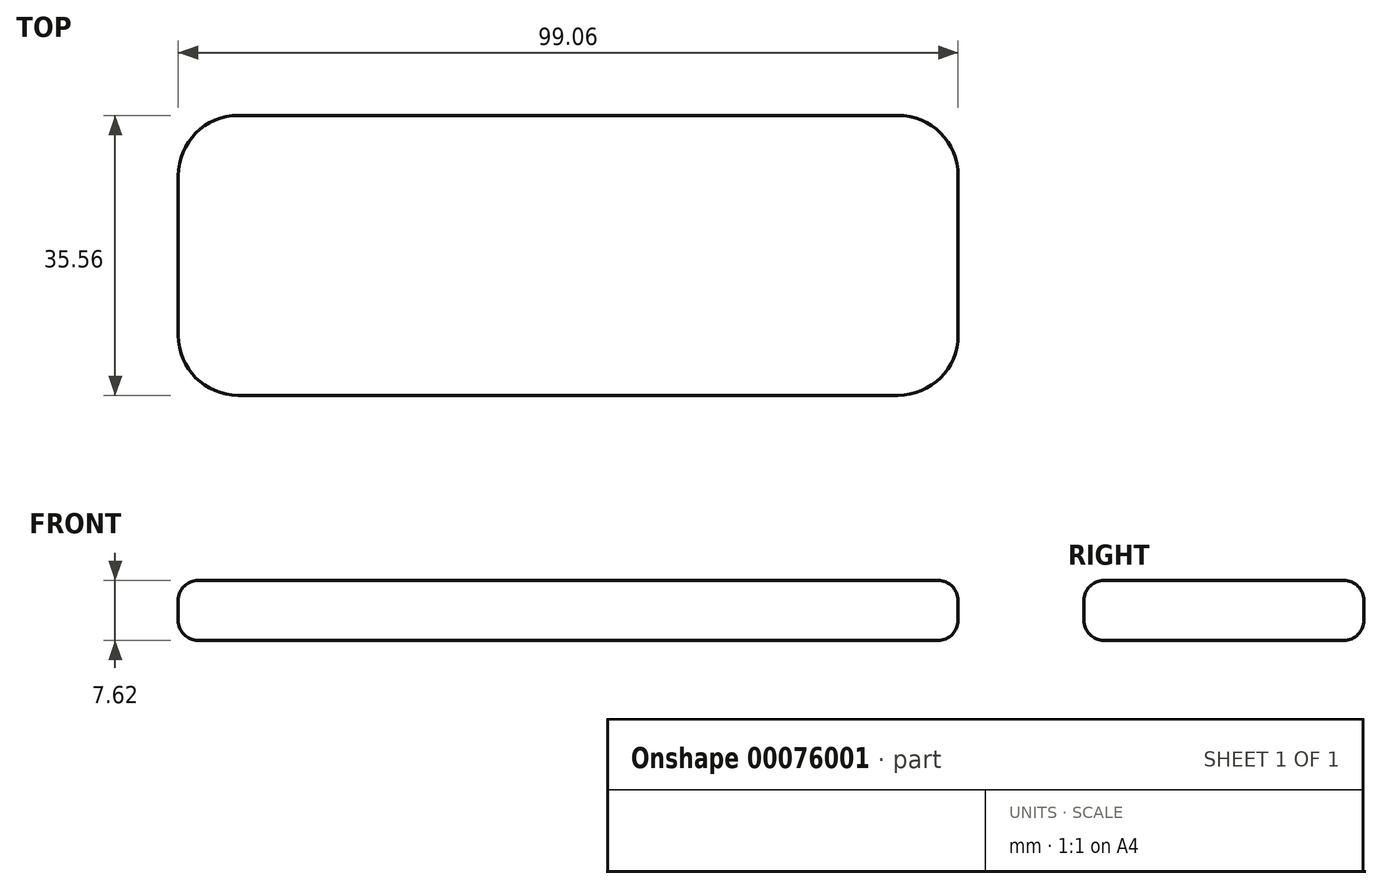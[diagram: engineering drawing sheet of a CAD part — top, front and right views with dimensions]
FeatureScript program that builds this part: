
annotation { "Feature Type Name" : "Feature", "Feature Type Description" : "" }
export const myFeature = defineFeature(function(context is Context, id is Id, definition is map)
    precondition{}
    {
        {
            var Q0;
            Q0=qCreatedBy(makeId("Top.planeOp"),FACE);
            var sketch = newSketch(context, id + "F0", { "sketchPlane" : qUnion([Q0])});
            skLineSegment(sketch, "E0.bottom", {"start": v(49.53, -17.78) * mm, "end": v(-49.53, -17.78) * mm});
            skLineSegment(sketch, "E0.top", {"start": v(49.53, 17.78) * mm, "end": v(-49.53, 17.78) * mm});
            skLineSegment(sketch, "E0.left", {"start": v(49.53, -17.78) * mm, "end": v(49.53, 17.78) * mm});
            skLineSegment(sketch, "E0.right", {"start": v(-49.53, -17.78) * mm, "end": v(-49.53, 17.78) * mm});
            skPoint(sketch, "E0.middle", {"position": v(0, 0) * mm});
            skSolve(sketch);
        }
        {
            var Q0;
            Q0=makeQuery(id+"F0.imprint","IMPRINT",FACE,{"disambiguationData":[TD([[makeQuery(id+"F0.imprint","IMPRINT",EDGE,{"derivedFrom":sQuery(id+"F0.wireOp",EDGE,"E0.bottom")}),-1.0]])]});
            extrude(context, id + "F1", {"entities" : qUnion([Q0]), "depth" : 7.62 * mm});
        }
        {
            var Q0;
            Q0=makeQuery(id+"F1.opExtrude","SWEPT_EDGE",EDGE,{"disambiguationData":[OSD([sQuery(id+"F0.wireOp",EDGE,"E0.bottom"),sQuery(id+"F0.wireOp",EDGE,"E0.left")])]});
            var Q1;
            Q1=makeQuery(id+"F1.opExtrude","SWEPT_EDGE",EDGE,{"disambiguationData":[OSD([sQuery(id+"F0.wireOp",EDGE,"E0.top"),sQuery(id+"F0.wireOp",EDGE,"E0.left")])]});
            var Q2;
            Q2=makeQuery(id+"F1.opExtrude","SWEPT_EDGE",EDGE,{"disambiguationData":[OSD([sQuery(id+"F0.wireOp",EDGE,"E0.bottom"),sQuery(id+"F0.wireOp",EDGE,"E0.right")])]});
            var Q3;
            Q3=makeQuery(id+"F1.opExtrude","SWEPT_EDGE",EDGE,{"disambiguationData":[OSD([sQuery(id+"F0.wireOp",EDGE,"E0.top"),sQuery(id+"F0.wireOp",EDGE,"E0.right")])]});
            fillet(context, id + "F2", {"entities" : qUnion([Q0, Q1, Q2, Q3]), "radius" : 7.62 * mm, "tangentPropagation" : true, "allowEdgeOverflow" : false});
        }
        {
            var Q0;
            Q0=makeQuery(id+"F1.opExtrude","CAP_FACE",FACE,{"disambiguationData":[OSD([sQuery(id+"F0.wireOp",EDGE,"E0.bottom"),sQuery(id+"F0.wireOp",EDGE,"E0.top"),sQuery(id+"F0.wireOp",EDGE,"E0.left"),sQuery(id+"F0.wireOp",EDGE,"E0.right")])],"isStart":false});
            var Q1;
            Q1=makeQuery(id+"F1.opExtrude","CAP_FACE",FACE,{"disambiguationData":[OSD([sQuery(id+"F0.wireOp",EDGE,"E0.bottom"),sQuery(id+"F0.wireOp",EDGE,"E0.top"),sQuery(id+"F0.wireOp",EDGE,"E0.left"),sQuery(id+"F0.wireOp",EDGE,"E0.right")])],"isStart":true});
            fillet(context, id + "F3", {"entities" : qUnion([Q0, Q1]), "radius" : 2.54 * mm, "tangentPropagation" : true, "allowEdgeOverflow" : false});
        }
    });
